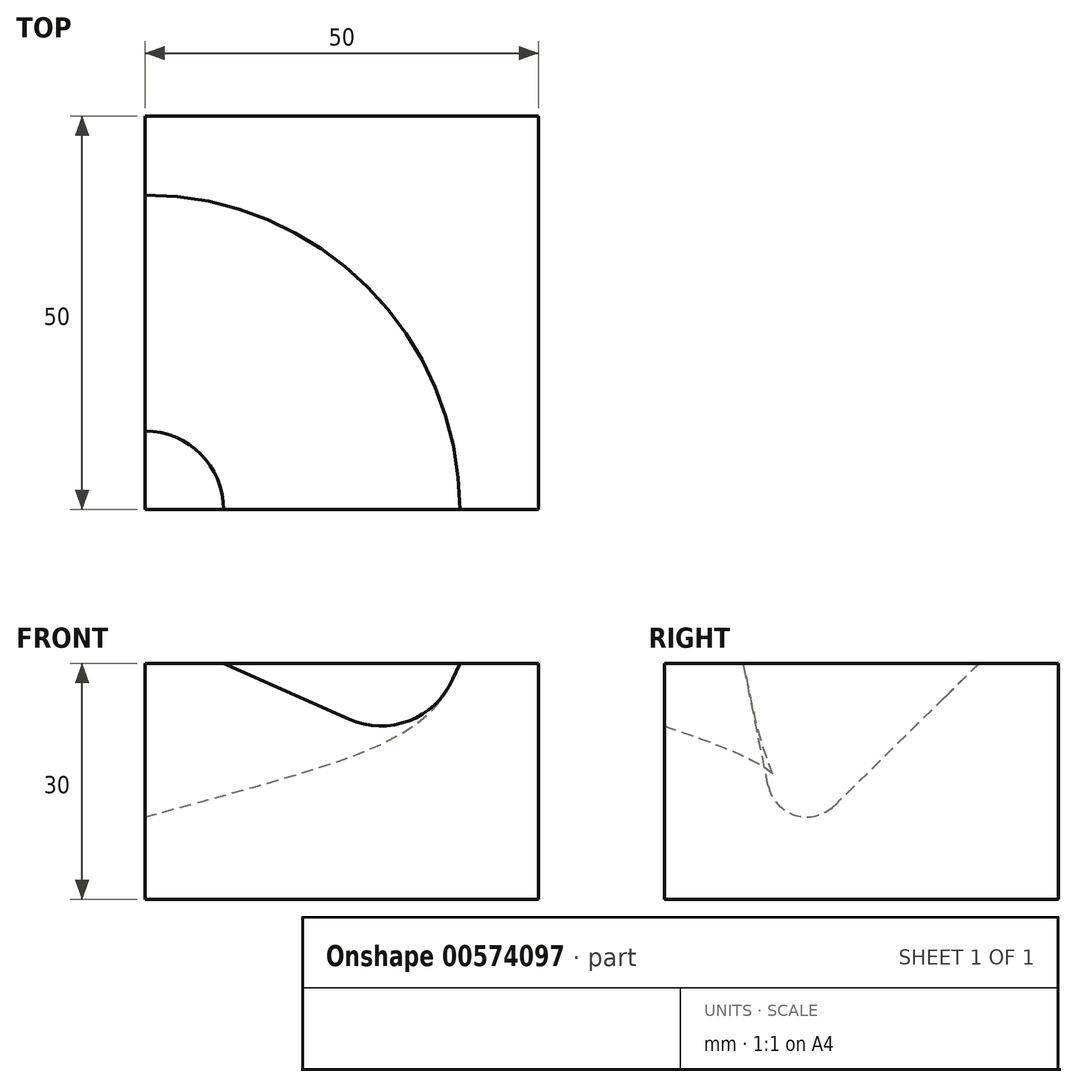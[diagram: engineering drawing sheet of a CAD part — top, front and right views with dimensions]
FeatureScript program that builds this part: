
annotation { "Feature Type Name" : "Feature", "Feature Type Description" : "" }
export const myFeature = defineFeature(function(context is Context, id is Id, definition is map)
    precondition{}
    {
        {
            var Q0;
            Q0=qCreatedBy(makeId("Top.planeOp"),FACE);
            var sketch = newSketch(context, id + "F0", { "sketchPlane" : qUnion([Q0])});
            skLineSegment(sketch, "E0.bottom", {"start": v(25, -25) * mm, "end": v(-25, -25) * mm});
            skLineSegment(sketch, "E0.top", {"start": v(25, 25) * mm, "end": v(-25, 25) * mm});
            skLineSegment(sketch, "E0.left", {"start": v(25, -25) * mm, "end": v(25, 25) * mm});
            skLineSegment(sketch, "E0.right", {"start": v(-25, -25) * mm, "end": v(-25, 25) * mm});
            skPoint(sketch, "E0.middle", {"position": v(0, 0) * mm});
            skSolve(sketch);
        }
        {
            var Q0;
            Q0=makeQuery(id+"F0.imprint","IMPRINT",FACE,{"disambiguationData":[TD([[makeQuery(id+"F0.imprint","IMPRINT",EDGE,{"derivedFrom":sQuery(id+"F0.wireOp",EDGE,"E0.bottom")}),-1.0]])]});
            extrude(context, id + "F1", {"entities" : qUnion([Q0]), "depth" : 30 * mm, "offsetDistance" : 25 * mm});
        }
        {
            var Q0;
            Q0=makeQuery(id+"F1.opExtrude","SWEPT_FACE",FACE,{"disambiguationData":[OSD([sQuery(id+"F0.wireOp",EDGE,"E0.right")])]});
            var sketch = newSketch(context, id + "F2", { "sketchPlane" : qUnion([Q0])});
            skLineSegment(sketch, "E1", {"start": v(-15, 30) * mm, "end": v(3.43, 11.9) * mm});
            skLineSegment(sketch, "E2", {"start": v(11.84, 14.48) * mm, "end": v(15, 30) * mm});
            skPoint(sketch, "E3.visualSharp", {"position": v(10, 5.46) * mm});
            skArc(sketch, "E3.filletArc", {"start": v(3.43, 11.9) * mm, "mid": v(8.4, 10.7) * mm, "end": v(11.84, 14.48) * mm});
            skSolve(sketch);
        }
        {
            var Q0;
            Q0=makeQuery(id+"F1.opExtrude","SWEPT_FACE",FACE,{"disambiguationData":[OSD([sQuery(id+"F0.wireOp",EDGE,"E0.bottom")])]});
            var sketch = newSketch(context, id + "F3", { "sketchPlane" : qUnion([Q0])});
            skLineSegment(sketch, "E4", {"start": v(-15, 30) * mm, "end": v(0.87, 22.9) * mm});
            skLineSegment(sketch, "E5", {"start": v(14.08, 27.95) * mm, "end": v(15, 30) * mm});
            skPoint(sketch, "E6.visualSharp", {"position": v(10, 18.82) * mm});
            skArc(sketch, "E6.filletArc", {"start": v(0.87, 22.9) * mm, "mid": v(8.52, 22.69) * mm, "end": v(14.08, 27.95) * mm});
            skSolve(sketch);
        }
        {
            var Q0;
            Q0=makeQuery(id+"F1.opExtrude","CAP_FACE",FACE,{"disambiguationData":[OSD([sQuery(id+"F0.wireOp",EDGE,"E0.bottom"),sQuery(id+"F0.wireOp",EDGE,"E0.top"),sQuery(id+"F0.wireOp",EDGE,"E0.left"),sQuery(id+"F0.wireOp",EDGE,"E0.right")])],"isStart":false});
            var sketch = newSketch(context, id + "F4", { "sketchPlane" : qUnion([Q0])});
            skLineSegment(sketch, "E7.bottom", {"start": v(15, -25) * mm, "end": v(-15, -25) * mm});
            skLineSegment(sketch, "E7.right", {"start": v(-25, -15) * mm, "end": v(-25, 15) * mm});
            skPoint(sketch, "E7.middle", {"position": v(0, 0) * mm});
            skArc(sketch, "E8", {"start": v(-15, -25) * mm, "mid": v(-17.93, -17.93) * mm, "end": v(-25, -15) * mm});
            skArc(sketch, "E9", {"start": v(15, -25) * mm, "mid": v(3.28, 3.28) * mm, "end": v(-25, 15) * mm});
            skPoint(sketch, "E7.left.start.orphan", {"position": v(25, -25) * mm});
            skPoint(sketch, "E7.top.start.orphan", {"position": v(25, 25) * mm});
            skPoint(sketch, "E10.orphan", {"position": v(-25, 25) * mm});
            skSolve(sketch);
        }
        {
            var Q1;
            {var subQ0=sQuery(id+"F2.wireOp",EDGE,"E1");Q1=makeQuery(id+"F2.imprint","IMPRINT",FACE,{"disambiguationData":[TD([[makeQuery(id+"F2.imprint","IMPRINT",EDGE,{"derivedFrom":subQ0}),1.0]])]});}
            var Q2;
            {var subQ0=sQuery(id+"F3.wireOp",EDGE,"E4");Q2=makeQuery(id+"F3.imprint","IMPRINT",FACE,{"disambiguationData":[TD([[makeQuery(id+"F3.imprint","IMPRINT",EDGE,{"derivedFrom":subQ0}),1.0]])]});}
            var Q3;
            Q3=sQuery(id+"F4.wireOp",EDGE,"E8");
            var Q4;
            Q4=sQuery(id+"F4.wireOp",EDGE,"E9");
            loft(context, id + "F5", {"operationType" : NewBodyOperationType.REMOVE, "addGuides" : true, "sheetProfilesArray" : [{ "sheetProfileEntities" : qUnion([Q1]) }, { "sheetProfileEntities" : qUnion([Q2]) }], "guidesArray" : [{ "guideEntities" : qUnion([Q3]), "guideDerivativeType" : LoftGuideDerivativeType.DEFAULT, "guideDerivativeMagnitude" : 1 }, { "guideEntities" : qUnion([Q4]), "guideDerivativeType" : LoftGuideDerivativeType.DEFAULT, "guideDerivativeMagnitude" : 1 }]});
        }
    });
